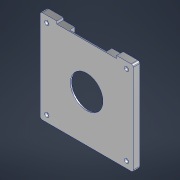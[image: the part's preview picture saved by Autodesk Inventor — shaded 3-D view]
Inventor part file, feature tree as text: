
AUTODESK INVENTOR PART (.ipt)
format: ipt  version: 2022 (Build 260153000, 153)  size: 155,648 bytes
history: native  units: mm
features: sketch x3, other x3, extrude x2, reference x2, hole x1, chamfer x1, projected_geometry x1
ambient origin geometry x8: Origin, YZ Plane, XZ Plane, XY Plane, X Axis, Y Axis, Z Axis, Center Point
bodies: Solid1 (feature_tree)
feature tree (13):
  extrude  "Extrusion1"  Depth=2.0mm TaperAngle=0.0deg
  extrude  "Extrusion2"  Depth=120.0mm
  hole  "Hole1"  [1 undecoded]
  chamfer  "Chamfer1"  [1 undecoded]
  sketch  "Sketch1"  dims[d0=8.0mm d1=0.0mm d2=2.0mm d3=0.0mm]
  reference  "Reference1"
  sketch  "Sketch2"  dims[d4=2.0mm d5=120.0mm]
  projected_geometry  "Projected Loop1"
  reference  "Reference2"
  sketch  "Sketch3"  dims[d7=3.4mm d8=6.0mm d9=6.5mm d10=3.4mm d11=90.0deg d12=8.8mm d13=20.594885mm d14=2.0mm d15=2.0mm d16=45.0deg]
  other  "Assembly2.iam"
  other  "Soporte:1"
  other  "BridaTornillo2:1"
note: 2 required parameter values undecoded (feature->parameter linkage not recoverable at this tier; creation-order binding heuristic only, values carry confidence <= 0.55)
